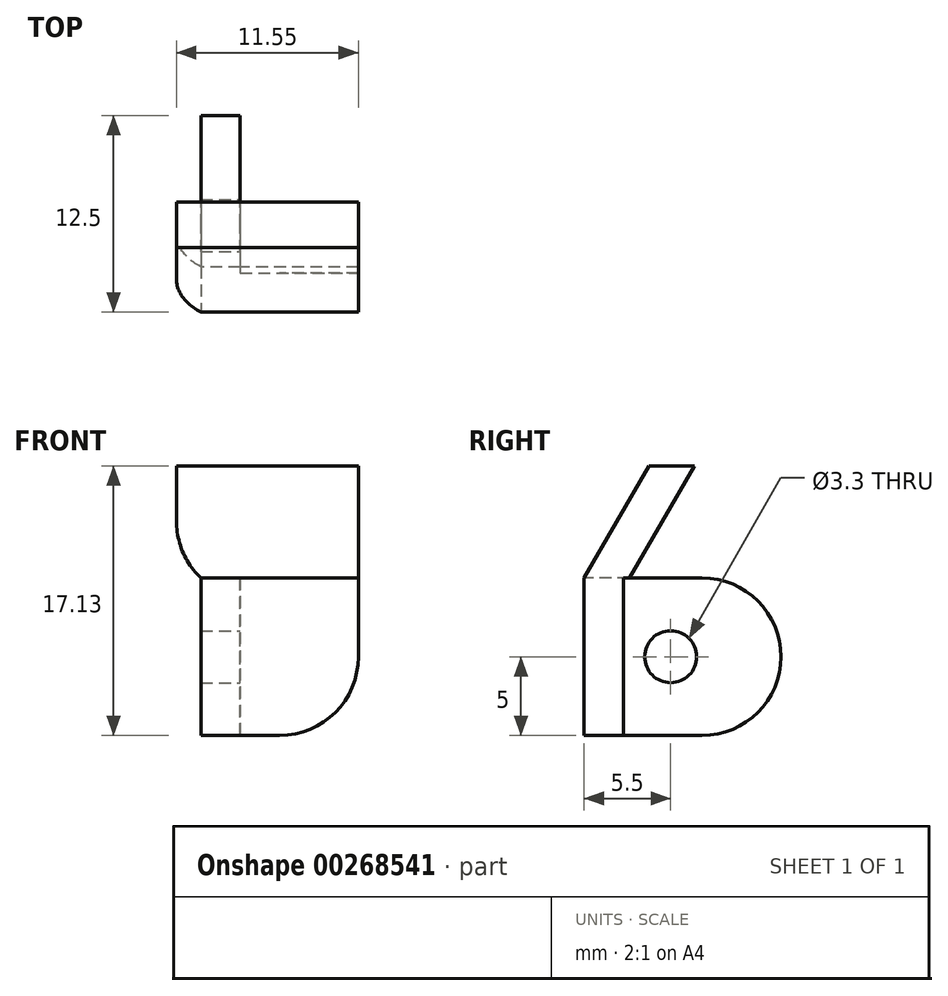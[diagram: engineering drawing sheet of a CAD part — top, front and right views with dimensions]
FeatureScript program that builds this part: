
annotation { "Feature Type Name" : "Feature", "Feature Type Description" : "" }
export const myFeature = defineFeature(function(context is Context, id is Id, definition is map)
    precondition{}
    {
        {
            var Q0;
            Q0=qCreatedBy(makeId("Top.planeOp"),FACE);
            var sketch = newSketch(context, id + "F0", { "sketchPlane" : qUnion([Q0])});
            skLineSegment(sketch, "E0.bottom", {"start": v(4.05, 18.68) * mm, "end": v(1.55, 18.68) * mm});
            skLineSegment(sketch, "E0.left", {"start": v(4.05, 18.68) * mm, "end": v(4.05, 8.68) * mm});
            skLineSegment(sketch, "E0.right", {"start": v(1.55, 18.68) * mm, "end": v(1.55, 8.68) * mm});
            skLineSegment(sketch, "E1.bottom", {"start": v(4.05, 8.68) * mm, "end": v(11.55, 8.68) * mm});
            skLineSegment(sketch, "E1.top", {"start": v(1.55, 6.18) * mm, "end": v(11.55, 6.18) * mm});
            skLineSegment(sketch, "E1.left", {"start": v(1.55, 8.68) * mm, "end": v(1.55, 6.18) * mm});
            skLineSegment(sketch, "E1.right", {"start": v(11.55, 8.68) * mm, "end": v(11.55, 6.18) * mm});
            skSolve(sketch);
        }
        {
            var Q0;
            Q0 = qSketchRegion(id + "F0", true);
            extrude(context, id + "F1", {"entities" : qUnion([Q0]), "depth" : 10 * mm});
        }
        {
            var Q0;
            Q0=makeQuery(id+"F1.opExtrude","SWEPT_FACE",FACE,{"disambiguationData":[OSD([sQuery(id+"F0.wireOp",EDGE,"E0.left")])]});
            var sketch = newSketch(context, id + "F2", { "sketchPlane" : qUnion([Q0])});
            skPoint(sketch, "E2", {"position": v(11.68, 5) * mm});
            skSolve(sketch);
        }
        {
            var Q0;
            Q0=qCreatedBy(makeId("Right.planeOp"),FACE);
            var sketch = newSketch(context, id + "F3", { "sketchPlane" : qUnion([Q0])});
            skLineSegment(sketch, "E3", {"start": v(6.18, 10) * mm, "end": v(10.3, 17.13) * mm});
            skLineSegment(sketch, "E4", {"start": v(10.3, 17.13) * mm, "end": v(13.18, 17.13) * mm});
            skLineSegment(sketch, "E5", {"start": v(13.18, 17.13) * mm, "end": v(9.07, 10) * mm});
            skLineSegment(sketch, "E6", {"start": v(9.07, 10) * mm, "end": v(6.18, 10) * mm});
            skSolve(sketch);
        }
        {
            var Q0;
            Q0 = qSketchRegion(id + "F3", true);
            var Q1;
            Q1=makeQuery(id+"F3.imprint","IMPRINT",FACE,{"disambiguationData":[TD([[makeQuery(id+"F3.imprint","IMPRINT",EDGE,{"derivedFrom":sQuery(id+"F3.wireOp",EDGE,"E3")}),-1.0]])]});
            var Q2;
            Q2=makeQuery(id+"F1.opExtrude","SWEPT_FACE",FACE,{"disambiguationData":[OSD([sQuery(id+"F0.wireOp",EDGE,"E1.right")])]});
            var Q3;
            Q3=makeQuery(id+"F1.opExtrude","SWEPT_FACE",FACE,{"disambiguationData":[OSD([sQuery(id+"F0.wireOp",EDGE,"E0.right"),sQuery(id+"F0.wireOp",EDGE,"E1.left")])]});
            extrude(context, id + "F4", {"entities" : qUnion([Q0, Q1]), "operationType" : NewBodyOperationType.ADD, "endBound" : BoundingType.UP_TO_SURFACE, "endBoundEntityFace" : qUnion([Q2]), "depth" : 25 * mm});
        }
        {
            var Q0;
            Q0=sQuery(id+"F2.wireOp",VERTEX,"E2");
            var Q1;
            Q1=makeQuery(id+"F1.opExtrude","SWEPT_BODY",BODY,{"disambiguationData":[OSD([sQuery(id+"F0.wireOp",EDGE,"E0.bottom"),sQuery(id+"F0.wireOp",EDGE,"E0.left"),sQuery(id+"F0.wireOp",EDGE,"E0.right"),sQuery(id+"F0.wireOp",EDGE,"E1.bottom"),sQuery(id+"F0.wireOp",EDGE,"E1.top"),sQuery(id+"F0.wireOp",EDGE,"E1.left"),sQuery(id+"F0.wireOp",EDGE,"E1.right")])]});
            hole(context, id + "F5", {"style" : HoleStyle.SIMPLE, "endStyle" : HoleEndStyle.THROUGH, "holeDiameter" : 3.3 * mm, "tappedDepth" : 12 * mm, "tapClearance" : 3, "locations" : qUnion([Q0]), "scope" : qUnion([Q1])});
        }
        {
            var Q0;
            Q0=makeQuery(id+"F1.opExtrude","CAP_EDGE",EDGE,{"disambiguationData":[OSD([sQuery(id+"F0.wireOp",EDGE,"E0.bottom")])],"isStart":true});
            var Q1;
            Q1=makeQuery(id+"F1.opExtrude","CAP_EDGE",EDGE,{"disambiguationData":[OSD([sQuery(id+"F0.wireOp",EDGE,"E0.bottom")])],"isStart":false});
            var Q2;
            Q2=makeQuery(id+"F1.opExtrude","CAP_EDGE",EDGE,{"disambiguationData":[OSD([sQuery(id+"F0.wireOp",EDGE,"E1.right")])],"isStart":true});
            var Q3;
            Q3=makeQuery(id+"F4.opExtrude","CAP_EDGE",EDGE,{"disambiguationData":[OSD([sQuery(id+"F3.wireOp",EDGE,"E6")])],"isStart":true});
            fillet(context, id + "F6", {"entities" : qUnion([Q0, Q1, Q2, Q3]), "radius" : 5 * mm, "tangentPropagation" : true, "allowEdgeOverflow" : false});
        }
    });
